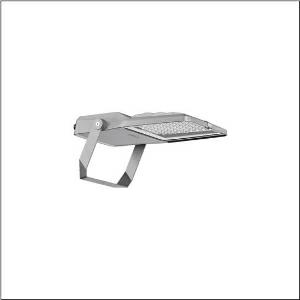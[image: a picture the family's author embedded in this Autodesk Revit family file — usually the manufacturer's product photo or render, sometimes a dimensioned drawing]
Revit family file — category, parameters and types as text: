
# Revit family: floodlight_fl_21_mini___pl61_5xa7776b2c1a_e1cc
name_source: partatom
category: Lighting Fixtures
units: mm (PartAtom-declared; Revit-internal decimal feet)

## family parameters
Cut with Voids When Loaded = No
Host = Face
Light Source = No
Part Type = Normal
Room Calculation Point = No
Round Connector Dimension = Use Diameter
Shared = No

## types (1)
- --- (1 x LED, 6110 lm, 45.7 W, 3000K)
    Apparent Load = 46 VA
    CIE Flux Codes = 33 65 98 100 100
    Color Rendering = 70
    Color Temperature = 3000K
    Default Elevation = 1800 mm
    Description = Floodlight FL 21 mini, floodlight, primary light control with lens, of PMMA, primary optical cover: protective disc, of toughened safety glass, transparent, light distribution: PL61, light emission: direct distribution, installation type: surface-mounted, LED, High Power LED, rated luminous flux: 6.110lm, luminous efficacy: 134lm/W, light colour: 730, colour temperature: 3000K, control gear: Smart Interface (Zhaga), control: flexible luminous flux parameterisation, time-dependent luminous flux control, constant luminous flux control, overheat protection, pre-setting: logarithmic dimming characteristic, with terminal, 6-pole, mains connection: 220..240V, AC, 50/60Hz, start of lifetime: 46W, end of service life: 48W, reduction: 22W, luminaire housing, of diecast aluminium, powder-coated, Siteco® metallic grey (DB 702S), corrosivity category C5 mid according to DIN EN ISO 12944, suitable for swimming pools, chlorine-resistant, sealing non-destructively replaceable, mounting bracket, of steel, galvanised, powder-coated, Siteco® metallic grey (DB 702S), Smart Interface below and above, protection rating (complete): IP66, insulation class (complete): insulation class II (safety insulation), certification: CE, ENEC, VDE, protection symbol: D, impact resistance: IK08, permissible operating ambient temperature: -40..+40°C, permissible operating ambient temperature for outdoor applications: -40..+50°C, standard: DIN EN 12944, LABS conformity tested according to VDMA 24364:2018-05, packaging unit: 1 piece

Light Distribution: PL61
    Height = 70 mm
    Lamp = 1 x LED
    Lamp Light Flux = 6110 lm
    Lamp Power = 45.7 W
    Lamp count = 1
    Length = 485 mm
    Luminous efficacy = 134 lm/W
    Manufacturer = Siteco
    ModVariant = No
    Model = 5XA7776B2C1A
    Number of Poles = 1
    OnlyDefault = Yes
    Power Factor = 1
    Product Name = Floodlight FL 21 mini | PL61
    Product group = floodlight | pylon annexe
    ProductGroupID = 6201
    Protection Class = Protection class II
    Protection Degree = IP 66
    RLX_Detail_Level = 1
    RLX_Emergency_Light_Flux = 0 lm
    RLX_Emergency_Type = 0
    RLX_Emergency_Type_DB = No
    RlxData = <blob elided: 96105 chars, md5=fc249d6d>
    Socket = socket
    Standby Power = 0 W
    System Light Flux = 6110 lm
    System Power = 46 W
    Type Comments = factory setting: luminous flux: 100 % | dim-lin: 254 | 463 mA
    Type Image = l_1006845.jpg
    URL = http://relux.com
    VarID = @adj_193633
    Voltage = 0 V
    Weight = 0.00 kg
    Width = 337 mm

## geometry (parser evidence)
native form markers: Blend x4, Sweep x12
no freeform markers — native parametric forms only
